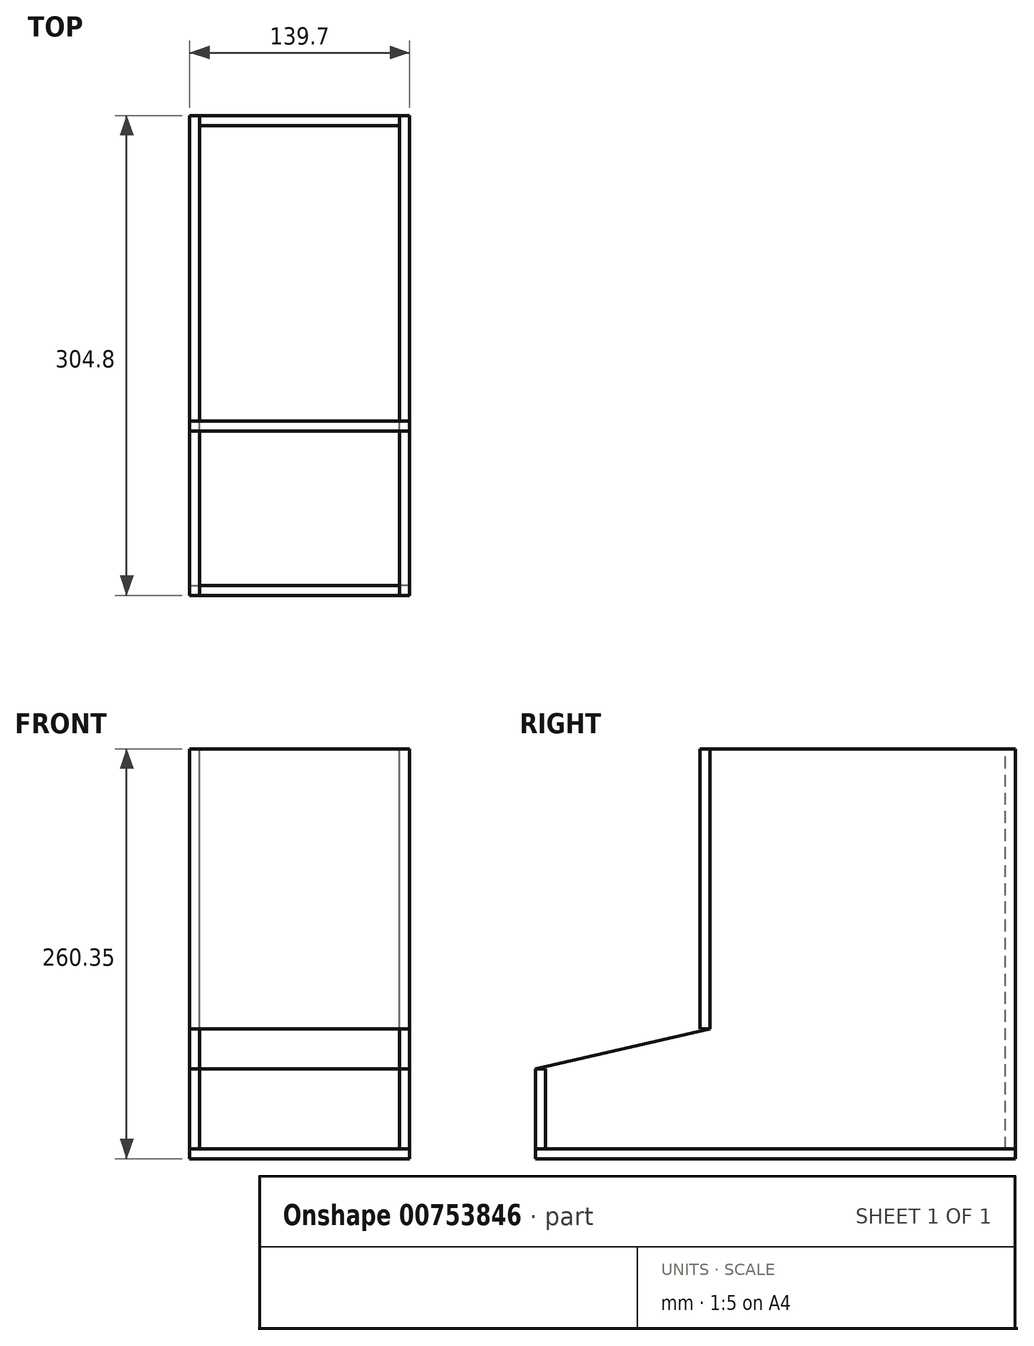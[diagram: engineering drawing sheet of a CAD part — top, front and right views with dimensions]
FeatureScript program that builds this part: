
annotation { "Feature Type Name" : "Feature", "Feature Type Description" : "" }
export const myFeature = defineFeature(function(context is Context, id is Id, definition is map)
    precondition{}
    {
        {
            var Q0;
            Q0=qCreatedBy(makeId("Front.planeOp"),FACE);
            var sketch = newSketch(context, id + "F0", { "sketchPlane" : qUnion([Q0])});
            skLineSegment(sketch, "E0.bottom", {"start": v(69.85, -3.17) * mm, "end": v(-69.85, -3.18) * mm});
            skLineSegment(sketch, "E0.top", {"start": v(69.85, 3.18) * mm, "end": v(-69.85, 3.17) * mm});
            skLineSegment(sketch, "E0.left", {"start": v(69.85, -3.17) * mm, "end": v(69.85, 3.18) * mm});
            skLineSegment(sketch, "E0.right", {"start": v(-69.85, -3.18) * mm, "end": v(-69.85, 3.17) * mm});
            skPoint(sketch, "E0.middle", {"position": v(0, 0) * mm});
            skLineSegment(sketch, "E1.bottom", {"start": v(-63.5, 3.18) * mm, "end": v(63.5, 3.18) * mm});
            skLineSegment(sketch, "E1.top", {"start": v(-63.5, 53.97) * mm, "end": v(63.5, 53.97) * mm});
            skLineSegment(sketch, "E1.left", {"start": v(-63.5, 3.17) * mm, "end": v(-63.5, 53.97) * mm});
            skLineSegment(sketch, "E1.right", {"start": v(63.5, 3.18) * mm, "end": v(63.5, 53.97) * mm});
            skSolve(sketch);
        }
        {
            var Q0;
            Q0=makeQuery(id+"F0.imprint","IMPRINT",FACE,{"disambiguationData":[TD([[makeQuery(id+"F0.imprint","IMPRINT",EDGE,{"derivedFrom":sQuery(id+"F0.wireOp",EDGE,"E0.bottom")}),-1.0]])]});
            extrude(context, id + "F1", {"entities" : qUnion([Q0]), "oppositeDirection" : true, "depth" : 304.8 * mm, "offsetDistance" : 25.4 * mm});
        }
        {
            var Q0;
            Q0=makeQuery(id+"F0.imprint","IMPRINT",FACE,{"disambiguationData":[TD([[makeQuery(id+"F0.imprint","IMPRINT",EDGE,{"derivedFrom":sQuery(id+"F0.wireOp",EDGE,"E1.top")}),-1.0]])]});
            extrude(context, id + "F2", {"entities" : qUnion([Q0]), "oppositeDirection" : true, "depth" : 6.35 * mm, "offsetDistance" : 25.4 * mm});
        }
        {
            var Q0;
            Q0=makeQuery(id+"F1.opExtrude","CAP_FACE",FACE,{"disambiguationData":[OSD([sQuery(id+"F0.wireOp",EDGE,"E0.bottom"),sQuery(id+"F0.wireOp",EDGE,"E0.top"),sQuery(id+"F0.wireOp",EDGE,"E0.left"),sQuery(id+"F0.wireOp",EDGE,"E0.right")])],"isStart":false});
            var sketch = newSketch(context, id + "F3", { "sketchPlane" : qUnion([Q0])});
            skLineSegment(sketch, "E2.bottom", {"start": v(-63.5, 3.18) * mm, "end": v(63.5, 3.18) * mm});
            skLineSegment(sketch, "E2.top", {"start": v(-63.5, 257.18) * mm, "end": v(63.5, 257.18) * mm});
            skLineSegment(sketch, "E2.left", {"start": v(-63.5, 3.18) * mm, "end": v(-63.5, 257.18) * mm});
            skLineSegment(sketch, "E2.right", {"start": v(63.5, 3.18) * mm, "end": v(63.5, 257.18) * mm});
            skSolve(sketch);
        }
        {
            var Q0;
            Q0 = qSketchRegion(id + "F3", true);
            extrude(context, id + "F4", {"entities" : qUnion([Q0]), "operationType" : NewBodyOperationType.ADD, "oppositeDirection" : true, "depth" : 6.35 * mm, "offsetDistance" : 25.4 * mm});
        }
        {
            var Q0;
            Q0=qCreatedBy(makeId("Right.planeOp"),FACE);
            cPlane(context, id + "F5", {"entities" : qUnion([Q0]), "cplaneType" : CPlaneType.OFFSET, "offset" : 63.5 * mm, "width" : 152.4 * mm, "height" : 152.4 * mm});
        }
        {
            var Q0;
            Q0=qCreatedBy(id+"F5.planeOp",FACE);
            var sketch = newSketch(context, id + "F6", { "sketchPlane" : qUnion([Q0])});
            skLineSegment(sketch, "E3.0.0", {"start": v(0, 3.18) * mm, "end": v(0, -3.17) * mm});
            skLineSegment(sketch, "E3.0.1", {"start": v(0, -3.17) * mm, "end": v(304.8, -3.17) * mm});
            skLineSegment(sketch, "E3.0.2", {"start": v(304.8, -3.17) * mm, "end": v(304.8, 3.18) * mm});
            skLineSegment(sketch, "E3.0.3", {"start": v(304.8, 3.18) * mm, "end": v(0, 3.18) * mm});
            skLineSegment(sketch, "E4.0.0", {"start": v(0, 53.97) * mm, "end": v(0, 3.18) * mm});
            skLineSegment(sketch, "E4.0.1", {"start": v(0, 3.18) * mm, "end": v(6.35, 3.18) * mm});
            skLineSegment(sketch, "E4.0.2", {"start": v(6.35, 3.18) * mm, "end": v(6.35, 53.97) * mm});
            skLineSegment(sketch, "E4.0.3", {"start": v(6.35, 53.97) * mm, "end": v(0, 53.97) * mm});
            skLineSegment(sketch, "E5.0.0", {"start": v(304.8, 3.18) * mm, "end": v(304.8, 257.18) * mm});
            skLineSegment(sketch, "E5.0.1", {"start": v(304.8, 257.18) * mm, "end": v(298.45, 257.18) * mm});
            skLineSegment(sketch, "E5.0.3", {"start": v(298.45, 3.18) * mm, "end": v(304.8, 3.18) * mm});
            skLineSegment(sketch, "E6", {"start": v(0, 53.97) * mm, "end": v(110.74, 79.37) * mm});
            skLineSegment(sketch, "E7", {"start": v(110.74, 79.37) * mm, "end": v(110.74, 257.18) * mm});
            skLineSegment(sketch, "E8", {"start": v(304.8, 257.18) * mm, "end": v(110.74, 257.18) * mm});
            skLineSegment(sketch, "E9", {"start": v(304.8, 257.18) * mm, "end": v(304.8, 3.18) * mm});
            skLineSegment(sketch, "E10", {"start": v(0, 3.18) * mm, "end": v(0, 53.97) * mm});
            skSolve(sketch);
        }
        {
            var Q0;
            Q0=makeQuery(id+"F6.imprint","IMPRINT",FACE,{"disambiguationData":[TD([[makeQuery(id+"F6.imprint","IMPRINT",EDGE,{"derivedFrom":sQuery(id+"F6.wireOp",EDGE,"E3.0.3")}),-1.0]])]});
            extrude(context, id + "F7", {"entities" : qUnion([Q0]), "depth" : 6.35 * mm, "offsetDistance" : 25.4 * mm});
        }
        {
            var Q0;
            Q0=makeQuery(id+"F7.opExtrude","SWEPT_BODY",BODY,{"disambiguationData":[OSD([sQuery(id+"F6.wireOp",EDGE,"E3.0.3"),sQuery(id+"F6.wireOp",EDGE,"E4.0.2"),sQuery(id+"F6.wireOp",EDGE,"E4.0.3"),sQuery(id+"F6.wireOp",EDGE,"E5.0.2"),sQuery(id+"F6.wireOp",EDGE,"E6"),sQuery(id+"F6.wireOp",EDGE,"E7"),sQuery(id+"F6.wireOp",EDGE,"E8")])]});
            var Q1;
            Q1=qCreatedBy(makeId("Right.planeOp"),FACE);
            mirror(context, id + "F8", {"entities" : qUnion([Q0]), "mirrorPlane" : qUnion([Q1])});
        }
        {
            var Q0;
            Q0=makeQuery(id+"F8.opPattern","COPY",FACE,{"derivedFrom":makeQuery(id+"F7.opExtrude","SWEPT_FACE",FACE,{"disambiguationData":[OSD([sQuery(id+"F6.wireOp",EDGE,"E7")])]}),"instanceName":"1"});
            var sketch = newSketch(context, id + "F9", { "sketchPlane" : qUnion([Q0])});
            skLineSegment(sketch, "E11.bottom", {"start": v(-69.85, 257.18) * mm, "end": v(69.85, 257.18) * mm});
            skLineSegment(sketch, "E11.top", {"start": v(-69.85, 79.37) * mm, "end": v(69.85, 79.37) * mm});
            skLineSegment(sketch, "E11.left", {"start": v(-69.85, 257.17) * mm, "end": v(-69.85, 79.38) * mm});
            skLineSegment(sketch, "E11.right", {"start": v(69.85, 257.17) * mm, "end": v(69.85, 79.37) * mm});
            skSolve(sketch);
        }
        {
            var Q0;
            Q0 = qSketchRegion(id + "F9", true);
            extrude(context, id + "F10", {"entities" : qUnion([Q0]), "depth" : 6.35 * mm, "offsetDistance" : 25.4 * mm});
        }
    });
